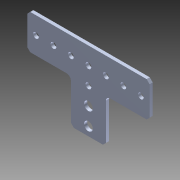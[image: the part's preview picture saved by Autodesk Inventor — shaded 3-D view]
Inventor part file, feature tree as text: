
AUTODESK INVENTOR PART (.ipt)
format: ipt  version: 2015 SP1 (Build 190203100, 203)  size: 153,088 bytes
history: native  units: in
note: dims shown in document units (in); Inventor stores cm internally (conversion verified against a paired STEP export)
features: fillet x1, other x1, extrude x1, imported_body x1, sketch x1, projected_geometry x1
ambient origin geometry x8: Origin, YZ Plane, XZ Plane, XY Plane, X Axis, Y Axis, Z Axis, Center Point
bodies: Body1 (feature_tree)
feature tree (6):
  fillet  "Fillet1"  Radius=0.25in
  other  "VersaFrame Gusset (217-3557)1"
  extrude  "Extrusion1"  Depth=1.0in TaperAngle=0.0deg
  imported_body  "Base1"
  sketch  "Sketch1"  dims[d1=0.25in d2=1.0in d3=0.0in]
  projected_geometry  "Projected Loop1"
